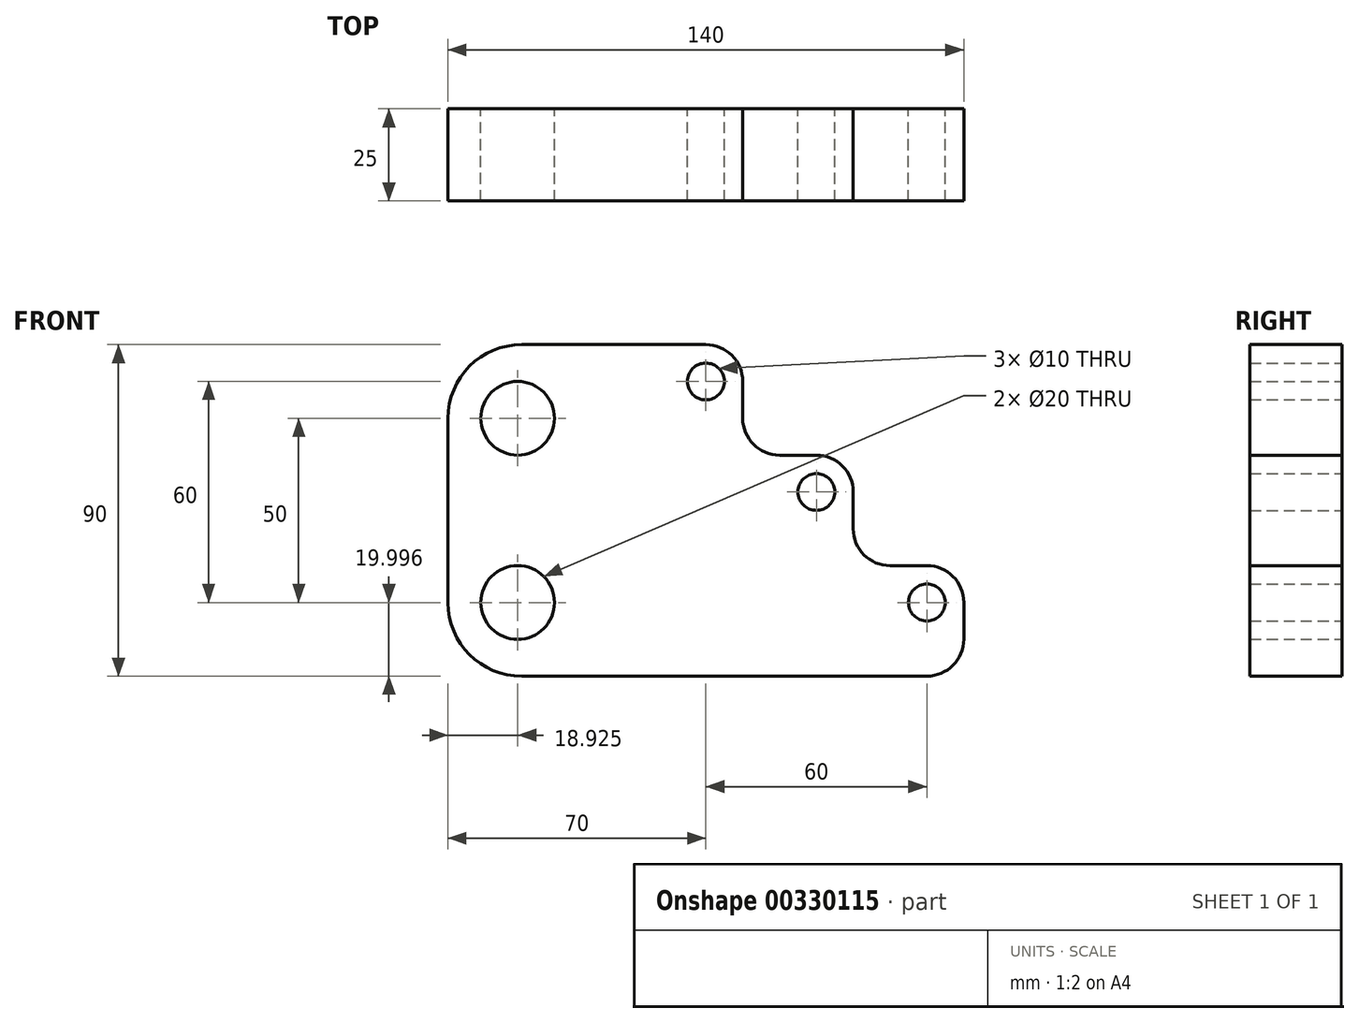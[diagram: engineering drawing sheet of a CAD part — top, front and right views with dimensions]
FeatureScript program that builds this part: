
annotation { "Feature Type Name" : "Feature", "Feature Type Description" : "" }
export const myFeature = defineFeature(function(context is Context, id is Id, definition is map)
    precondition{}
    {
        {
            var Q0;
            Q0=qCreatedBy(makeId("Front.planeOp"),FACE);
            var sketch = newSketch(context, id + "F0", { "sketchPlane" : qUnion([Q0])});
            skLineSegment(sketch, "E0", {"start": v(-130, -54.93) * mm, "end": v(0, -54.93) * mm});
            skLineSegment(sketch, "E1", {"start": v(-130, -34.93) * mm, "end": v(-130, 15.07) * mm});
            skLineSegment(sketch, "E2", {"start": v(-110, 35.07) * mm, "end": v(-50, 35.07) * mm});
            skLineSegment(sketch, "E3", {"start": v(-50, 25.07) * mm, "end": v(-50, 15.07) * mm});
            skLineSegment(sketch, "E4", {"start": v(-40, 5.07) * mm, "end": v(-20, 5.07) * mm});
            skLineSegment(sketch, "E5", {"start": v(-20, -4.93) * mm, "end": v(-20, -14.93) * mm});
            skLineSegment(sketch, "E6", {"start": v(-10, -24.93) * mm, "end": v(0, -24.93) * mm});
            skLineSegment(sketch, "E7", {"start": v(10, -34.93) * mm, "end": v(10, -44.93) * mm});
            skLineSegment(sketch, "E8", {"start": v(-110, -54.93) * mm, "end": v(-110, -54.93) * mm});
            skCircle(sketch, "E9", {"center": v(-111.08, 15.07) * mm, "radius": 10 * mm});
            skCircle(sketch, "E10", {"center": v(-111.08, -34.93) * mm, "radius": 10 * mm});
            skLineSegment(sketch, "E11", {"start": v(-60, 35.07) * mm, "end": v(-60, 35.07) * mm});
            skLineSegment(sketch, "E12", {"start": v(-60, 35.07) * mm, "end": v(-60, 25.07) * mm});
            skLineSegment(sketch, "E13", {"start": v(-30, 5.07) * mm, "end": v(-30, 5.07) * mm});
            skPoint(sketch, "E14.end.orphan", {"position": v(-31.08, 0) * mm});
            skLineSegment(sketch, "E15", {"start": v(-30, 5.07) * mm, "end": v(-30, -4.93) * mm});
            skLineSegment(sketch, "E16", {"start": v(10, -24.93) * mm, "end": v(0, -24.93) * mm});
            skLineSegment(sketch, "E17", {"start": v(0, -24.93) * mm, "end": v(0, -34.93) * mm});
            skCircle(sketch, "E18", {"center": v(-60, 25.07) * mm, "radius": 5 * mm});
            skCircle(sketch, "E19", {"center": v(-30, -4.93) * mm, "radius": 5 * mm});
            skCircle(sketch, "E20", {"center": v(0, -34.93) * mm, "radius": 5 * mm});
            skPoint(sketch, "E21.visualSharp", {"position": v(-50, 35.07) * mm});
            skArc(sketch, "E21.filletArc", {"start": v(-50, 25.07) * mm, "mid": v(-52.93, 32.14) * mm, "end": v(-60, 35.07) * mm});
            skPoint(sketch, "E22.visualSharp", {"position": v(-50, 5.07) * mm});
            skArc(sketch, "E22.filletArc", {"start": v(-50, 15.07) * mm, "mid": v(-47.07, 8) * mm, "end": v(-40, 5.07) * mm});
            skPoint(sketch, "E23.visualSharp", {"position": v(-20, 5.07) * mm});
            skArc(sketch, "E23.filletArc", {"start": v(-20, -4.93) * mm, "mid": v(-22.93, 2.14) * mm, "end": v(-30, 5.07) * mm});
            skPoint(sketch, "E24.visualSharp", {"position": v(-20, -24.93) * mm});
            skArc(sketch, "E24.filletArc", {"start": v(-20, -14.93) * mm, "mid": v(-17.07, -22) * mm, "end": v(-10, -24.93) * mm});
            skPoint(sketch, "E25.visualSharp", {"position": v(10, -24.93) * mm});
            skArc(sketch, "E25.filletArc", {"start": v(10, -34.93) * mm, "mid": v(7.07, -27.86) * mm, "end": v(0, -24.93) * mm});
            skPoint(sketch, "E26.visualSharp", {"position": v(10, -54.93) * mm});
            skArc(sketch, "E26.filletArc", {"start": v(0, -54.93) * mm, "mid": v(7.07, -52) * mm, "end": v(10, -44.93) * mm});
            skPoint(sketch, "E27.visualSharp", {"position": v(-130, 35.07) * mm});
            skArc(sketch, "E27.filletArc", {"start": v(-110, 35.07) * mm, "mid": v(-124.14, 29.2) * mm, "end": v(-130, 15.07) * mm});
            skPoint(sketch, "E28.visualSharp", {"position": v(-130, -54.93) * mm});
            skArc(sketch, "E28.filletArc", {"start": v(-130, -34.93) * mm, "mid": v(-124.14, -49.08) * mm, "end": v(-110, -54.93) * mm});
            skSolve(sketch);
        }
        {
            var Q0;
            Q0=makeQuery(id+"F0.imprint","IMPRINT",FACE,{"disambiguationData":[TD([[makeQuery(id+"F0.imprint","IMPRINT",EDGE,{"derivedFrom":sQuery(id+"F0.wireOp",EDGE,"E1")}),-1.0]])]});
            extrude(context, id + "F1", {"entities" : qUnion([Q0]), "depth" : 25 * mm});
        }
    });
